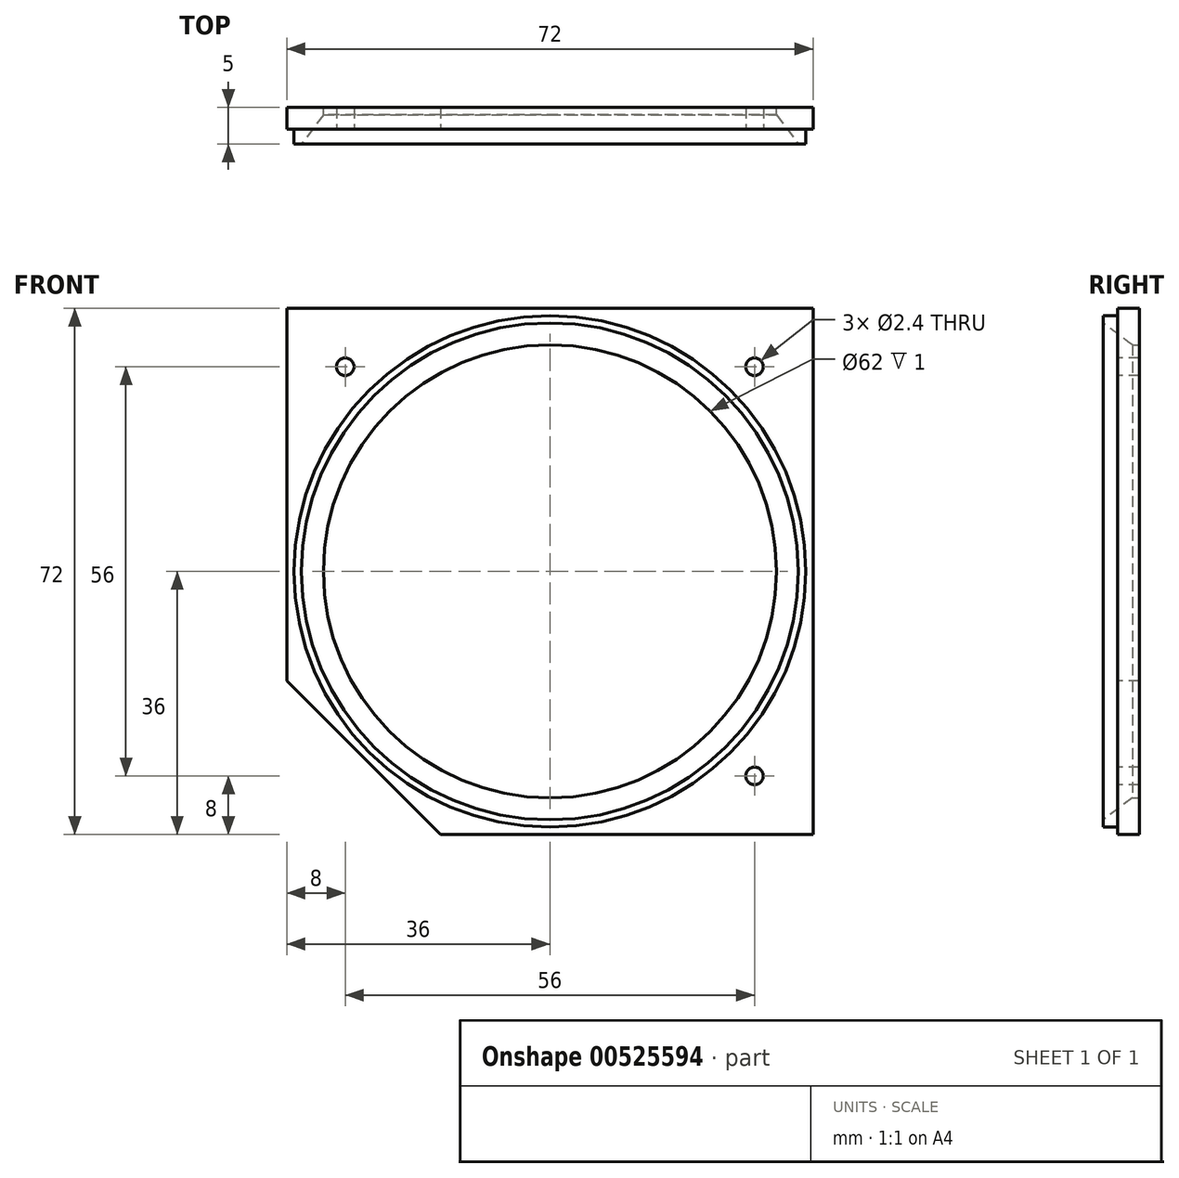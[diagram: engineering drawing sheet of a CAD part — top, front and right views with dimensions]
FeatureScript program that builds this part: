
annotation { "Feature Type Name" : "Feature", "Feature Type Description" : "" }
export const myFeature = defineFeature(function(context is Context, id is Id, definition is map)
    precondition{}
    {
        {
            var Q0;
            Q0=qCreatedBy(makeId("Right.planeOp"),FACE);
            var sketch = newSketch(context, id + "F0", { "sketchPlane" : qUnion([Q0])});
            skLineSegment(sketch, "E0", {"start": v(19.32, 0) * mm, "end": v(-16.11, 0) * mm, "construction": true});
            skLineSegment(sketch, "E1", {"start": v(-3, 35) * mm, "end": v(-3, 34) * mm});
            skLineSegment(sketch, "E2", {"start": v(2, 31) * mm, "end": v(2, 35) * mm});
            skLineSegment(sketch, "E3", {"start": v(2, 35) * mm, "end": v(-3, 35) * mm});
            skLineSegment(sketch, "E4", {"start": v(2, 31) * mm, "end": v(1, 31) * mm});
            skLineSegment(sketch, "E5", {"start": v(1, 31) * mm, "end": v(-3, 34) * mm});
            skSolve(sketch);
        }
        {
            var Q0;
            Q0=qSketchRegion(id+"F0",true);
            var Q1;
            Q1=sQuery(id+"F0.wireOp",EDGE,"E0");
            revolve(context, id + "F1", {"entities" : qUnion([Q0]), "axis" : qUnion([Q1]), "revolveType" : RevolveType.FULL});
        }
        {
            var Q0;
            Q0=makeQuery(id+"F1.opRevolve","SWEPT_FACE",FACE,{"disambiguationData":[OSD([sQuery(id+"F0.wireOp",EDGE,"E1")])]});
            cPlane(context, id + "F2", {"entities" : qUnion([Q0]), "cplaneType" : CPlaneType.OFFSET, "offset" : 2 * mm, "oppositeDirection" : true, "width" : 150 * mm, "height" : 150 * mm});
        }
        {
            var Q0;
            Q0=qCreatedBy(id+"F2.planeOp",FACE);
            var sketch = newSketch(context, id + "F3", { "sketchPlane" : qUnion([Q0])});
            skPoint(sketch, "E6.middle", {"position": v(0, 0) * mm});
            skCircle(sketch, "E7", {"center": v(-28, 28) * mm, "radius": 1.2 * mm});
            skCircle(sketch, "E8", {"center": v(-28, -28) * mm, "radius": 1.2 * mm, "construction": true});
            skCircle(sketch, "E9", {"center": v(28, -28) * mm, "radius": 1.2 * mm});
            skCircle(sketch, "E10", {"center": v(28, 28) * mm, "radius": 1.2 * mm});
            skCircle(sketch, "E11", {"center": v(0, 0) * mm, "radius": 35 * mm});
            skLineSegment(sketch, "E12.bottom", {"start": v(36, -36) * mm, "end": v(-15, -36) * mm});
            skLineSegment(sketch, "E12.top", {"start": v(36, 36) * mm, "end": v(-36, 36) * mm});
            skLineSegment(sketch, "E12.left", {"start": v(36, -36) * mm, "end": v(36, 36) * mm});
            skLineSegment(sketch, "E12.right", {"start": v(-36, -15) * mm, "end": v(-36, 36) * mm});
            skLineSegment(sketch, "E13", {"start": v(-36, -15) * mm, "end": v(-15, -36) * mm});
            skSolve(sketch);
        }
        {
            var Q0;
            Q0=qSketchRegion(id+"F3",true);
            extrude(context, id + "F4", {"entities" : qUnion([Q0]), "operationType" : NewBodyOperationType.ADD, "oppositeDirection" : true, "depth" : 3 * mm, "offsetDistance" : 25 * mm});
        }
    });
